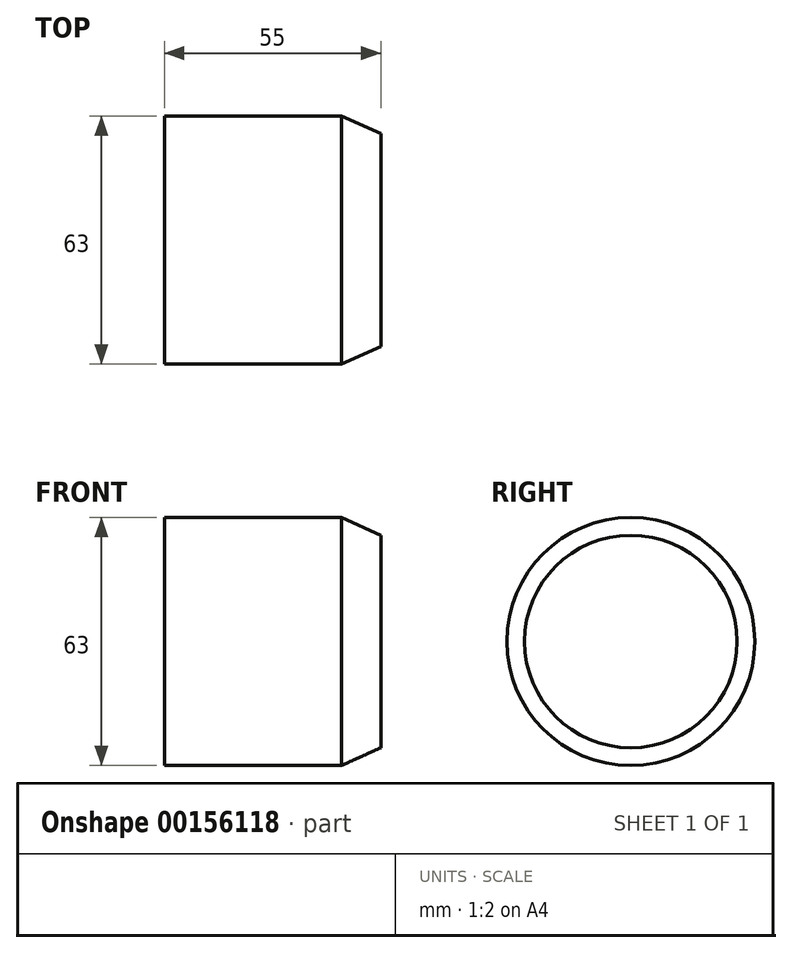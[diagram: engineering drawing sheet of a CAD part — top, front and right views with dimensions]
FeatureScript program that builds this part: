
annotation { "Feature Type Name" : "Feature", "Feature Type Description" : "" }
export const myFeature = defineFeature(function(context is Context, id is Id, definition is map)
    precondition{}
    {
        {
            var Q0;
            Q0=qCreatedBy(makeId("Front.planeOp"),FACE);
            var sketch = newSketch(context, id + "F0", { "sketchPlane" : qUnion([Q0])});
            skLineSegment(sketch, "E0", {"start": v(0, 0) * mm, "end": v(0, 31.5) * mm});
            skLineSegment(sketch, "E1", {"start": v(0, 31.5) * mm, "end": v(45, 31.5) * mm});
            skLineSegment(sketch, "E2", {"start": v(45, 31.5) * mm, "end": v(55, 27) * mm});
            skLineSegment(sketch, "E3", {"start": v(55, 27) * mm, "end": v(55, 0) * mm});
            skLineSegment(sketch, "E4", {"start": v(55, 0) * mm, "end": v(0, 0) * mm});
            skSolve(sketch);
        }
        {
            var Q0;
            Q0=makeQuery(id+"F0.imprint","IMPRINT",FACE,{"disambiguationData":[TD([[makeQuery(id+"F0.imprint","IMPRINT",EDGE,{"derivedFrom":sQuery(id+"F0.wireOp",EDGE,"E0")}),-1.0]])]});
            var Q1;
            Q1=sQuery(id+"F0.wireOp",EDGE,"E4");
            revolve(context, id + "F1", {"entities" : qUnion([Q0]), "axis" : qUnion([Q1]), "revolveType" : RevolveType.FULL});
        }
    });
